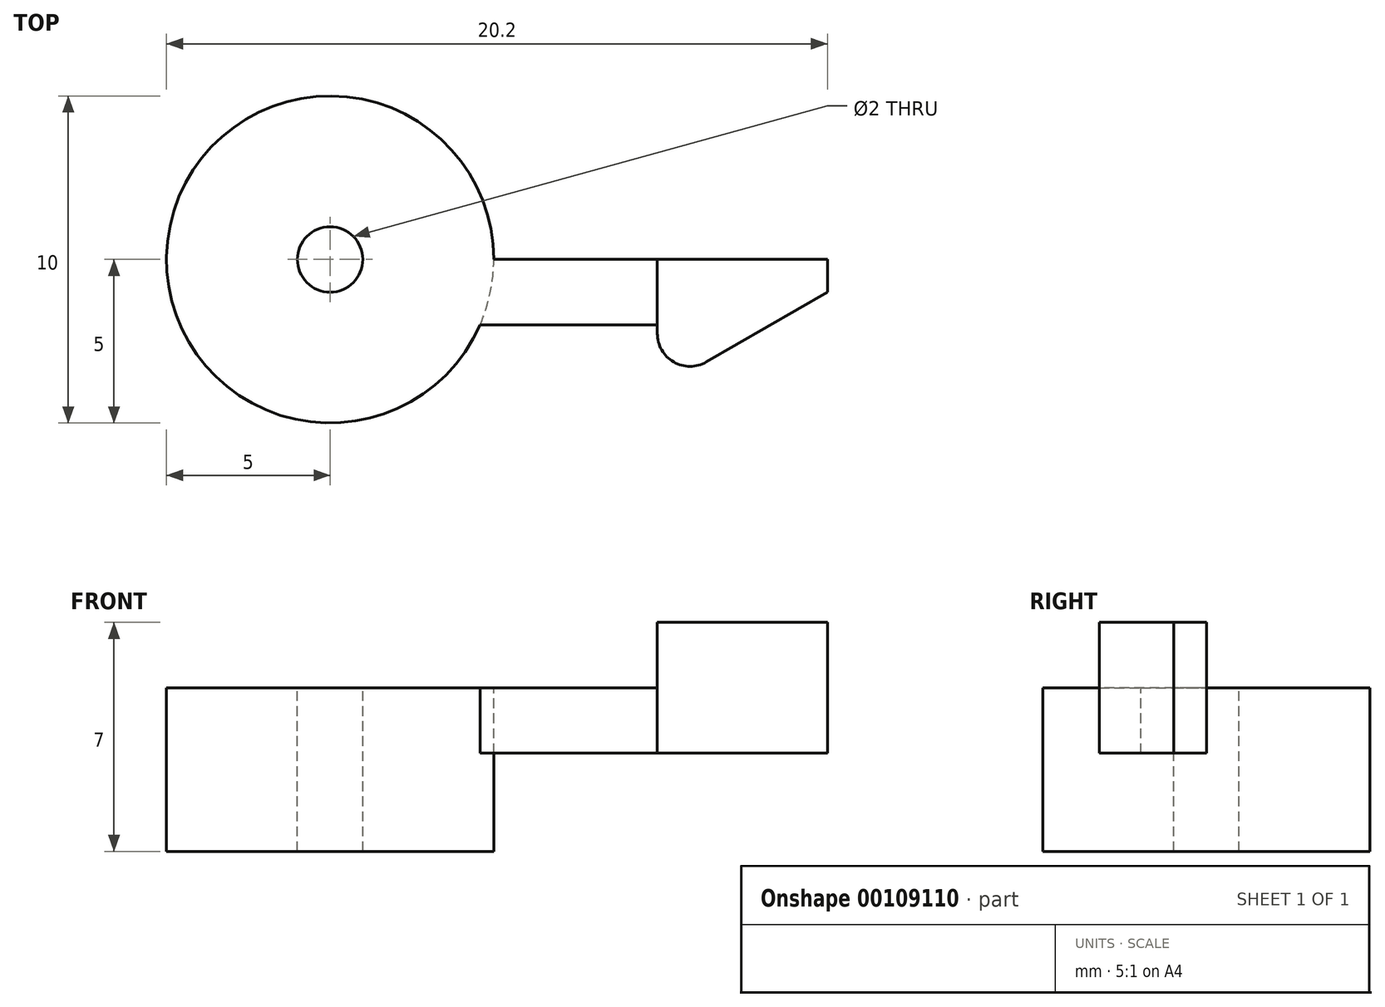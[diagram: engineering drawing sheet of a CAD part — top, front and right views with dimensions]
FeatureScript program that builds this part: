
annotation { "Feature Type Name" : "Feature", "Feature Type Description" : "" }
export const myFeature = defineFeature(function(context is Context, id is Id, definition is map)
    precondition{}
    {
        {
            var Q0;
            Q0=qCreatedBy(makeId("Top.planeOp"),FACE);
            var sketch = newSketch(context, id + "F0", { "sketchPlane" : qUnion([Q0])});
            skCircle(sketch, "E0", {"center": v(0, 0) * mm, "radius": 5 * mm});
            skLineSegment(sketch, "E1", {"start": v(5, 0) * mm, "end": v(15.2, 0) * mm});
            skLineSegment(sketch, "E2.MirrorCS", {"start": v(4.58, -2) * mm, "end": v(10, -2) * mm});
            skLineSegment(sketch, "E3.MirrorCS", {"start": v(10, -2) * mm, "end": v(10, 0) * mm});
            skLineSegment(sketch, "E4.MirrorCS", {"start": v(10, -2) * mm, "end": v(10, -4) * mm});
            skLineSegment(sketch, "E5.MirrorCS", {"start": v(10, -4) * mm, "end": v(15.2, -1) * mm});
            skLineSegment(sketch, "E6.MirrorCS", {"start": v(15.2, -1) * mm, "end": v(15.2, 0) * mm});
            skSolve(sketch);
        }
        {
            var Q0;
            {var subQ0=sQuery(id+"F0.wireOp",EDGE,"E0");var subQ1=makeQuery(id+"F0.imprint","INTERSECT",VERTEX,{"derivedFrom":[subQ0,sQuery(id+"F0.wireOp",EDGE,"E2.MirrorCS")]});Q0=makeQuery(id+"F0.imprint","IMPRINT",FACE,{"disambiguationData":[TD([[makeQuery(id+"F0.imprint","IMPRINT",EDGE,{"disambiguationData":[TD([[subQ1,1.0]])],"derivedFrom":subQ0}),1.0]])]});}
            extrude(context, id + "F1", {"entities" : qUnion([Q0]), "oppositeDirection" : true, "depth" : 5 * mm});
        }
        {
            var Q0;
            {var subQ0=sQuery(id+"F0.wireOp",EDGE,"E2.MirrorCS");Q0=makeQuery(id+"F0.imprint","IMPRINT",FACE,{"disambiguationData":[TD([[makeQuery(id+"F0.imprint","IMPRINT",EDGE,{"derivedFrom":subQ0}),1.0]])]});}
            extrude(context, id + "F2", {"entities" : qUnion([Q0]), "operationType" : NewBodyOperationType.ADD, "oppositeDirection" : true, "depth" : 2 * mm});
        }
        {
            var Q0;
            {var subQ1=sQuery(id+"F0.wireOp",EDGE,"E3.MirrorCS");Q0=makeQuery(id+"F0.imprint","IMPRINT",FACE,{"disambiguationData":[TD([[makeQuery(id+"F0.imprint","IMPRINT",EDGE,{"derivedFrom":subQ1}),-1.0]])]});}
            extrude(context, id + "F3", {"entities" : qUnion([Q0]), "operationType" : NewBodyOperationType.ADD, "endBound" : BoundingType.SYMMETRIC, "depth" : 4 * mm});
        }
        {
            var Q0;
            Q0=makeQuery(id+"F3.opExtrude","SWEPT_EDGE",EDGE,{"disambiguationData":[OSD([sQuery(id+"F0.wireOp",EDGE,"E4.MirrorCS"),sQuery(id+"F0.wireOp",EDGE,"E5.MirrorCS")])]});
            fillet(context, id + "F4", {"entities" : qUnion([Q0]), "radius" : 1 * mm, "tangentPropagation" : true, "allowEdgeOverflow" : false});
        }
        {
            var Q0;
            Q0=sQuery(id+"F0.wireOp",VERTEX,"E0.center");
            var Q1;
            Q1=makeQuery(id+"F1.opExtrude","SWEPT_BODY",BODY,{"disambiguationData":[OSD([sQuery(id+"F0.wireOp",EDGE,"E0")])]});
            hole(context, id + "F5", {"style" : HoleStyle.SIMPLE, "endStyle" : HoleEndStyle.THROUGH, "holeDiameter" : 2 * mm, "locations" : qUnion([Q0]), "scope" : qUnion([Q1]), "isTappedThrough" : true});
        }
    });
